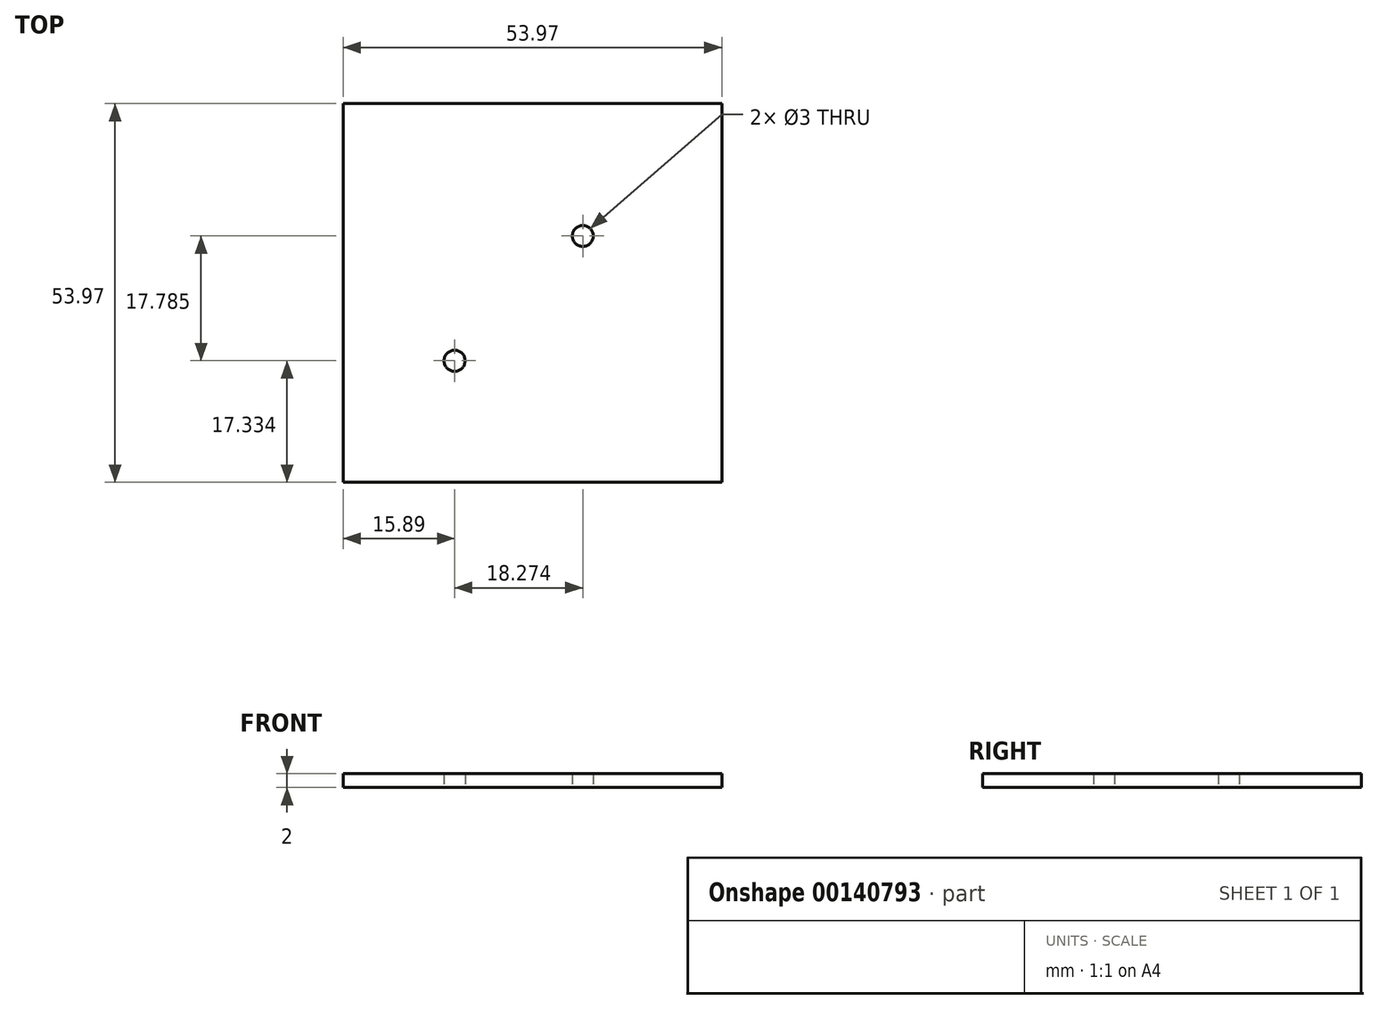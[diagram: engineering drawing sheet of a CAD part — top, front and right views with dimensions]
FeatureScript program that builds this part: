
annotation { "Feature Type Name" : "Feature", "Feature Type Description" : "" }
export const myFeature = defineFeature(function(context is Context, id is Id, definition is map)
    precondition{}
    {
        {
            var Q0;
            Q0=qCreatedBy(makeId("Top.planeOp"),FACE);
            var sketch = newSketch(context, id + "F0", { "sketchPlane" : qUnion([Q0])});
            skLineSegment(sketch, "E0", {"start": v(-50.76, 41.33) * mm, "end": v(-50.76, -12.64) * mm});
            skLineSegment(sketch, "E1", {"start": v(-50.76, -12.64) * mm, "end": v(3.21, -12.64) * mm});
            skLineSegment(sketch, "E2", {"start": v(3.21, -12.64) * mm, "end": v(3.21, 41.33) * mm});
            skLineSegment(sketch, "E3", {"start": v(-50.76, 41.33) * mm, "end": v(3.21, 41.33) * mm});
            skCircle(sketch, "E4", {"center": v(-34.87, 4.7) * mm, "radius": 1.5 * mm});
            skLineSegment(sketch, "E5", {"start": v(-34.87, 4.7) * mm, "end": v(-16.6, 22.48) * mm});
            skCircle(sketch, "E6", {"center": v(-16.6, 22.48) * mm, "radius": 1.5 * mm});
            skSolve(sketch);
        }
        {
            var Q0;
            Q0=makeQuery(id+"F0.imprint","IMPRINT",FACE,{"disambiguationData":[TD([[makeQuery(id+"F0.imprint","IMPRINT",EDGE,{"derivedFrom":sQuery(id+"F0.wireOp",EDGE,"E0")}),1.0]])]});
            extrude(context, id + "F1", {"entities" : qUnion([Q0]), "depth" : 2 * mm});
        }
    });
